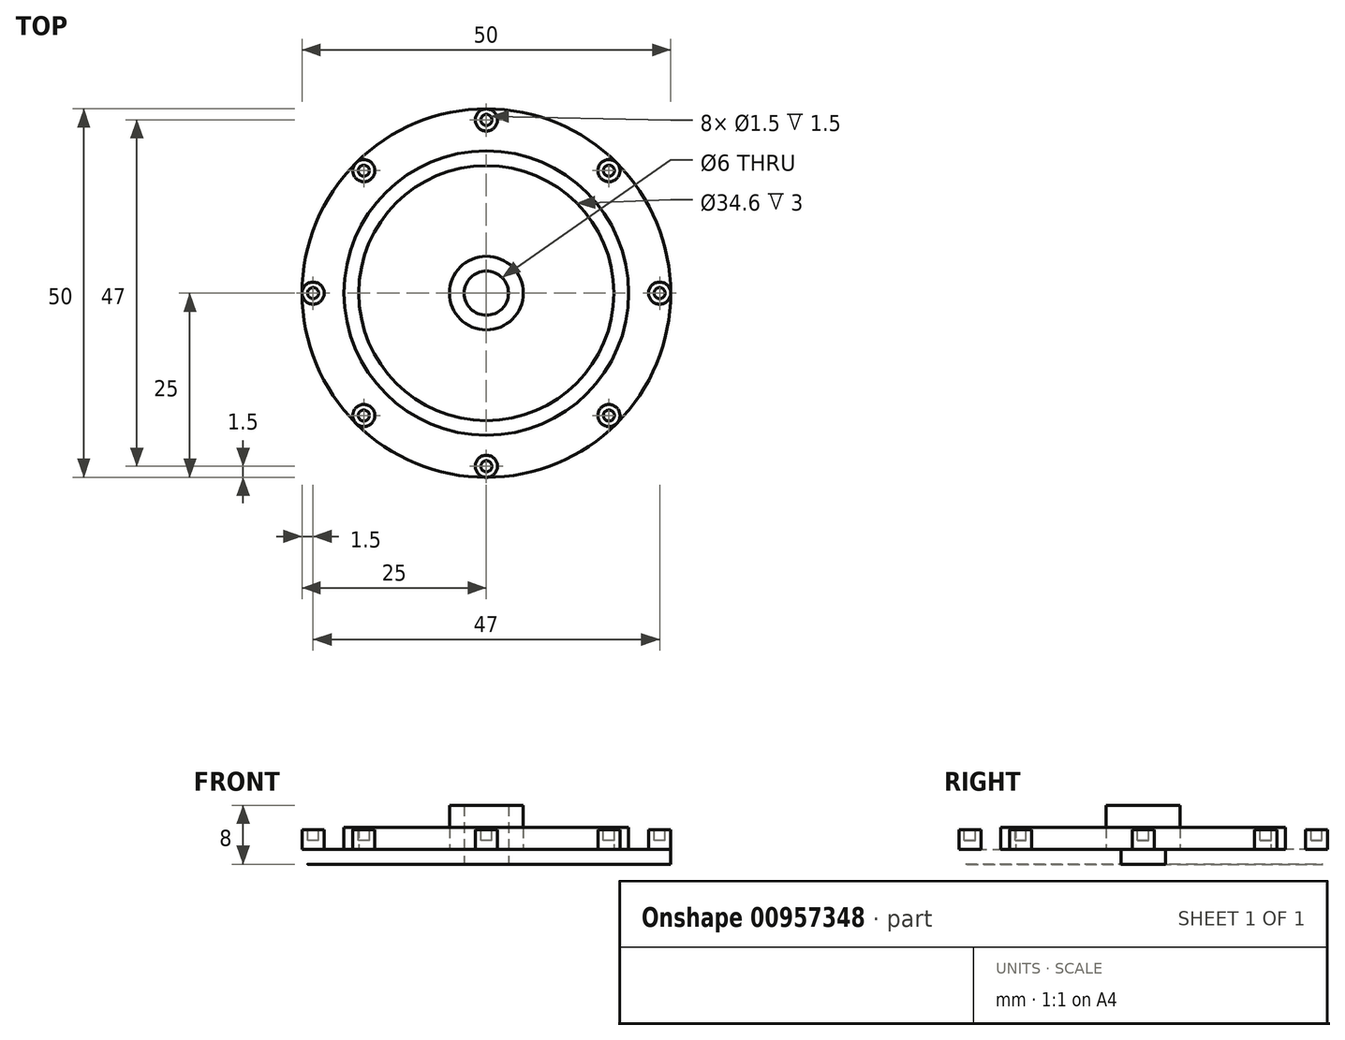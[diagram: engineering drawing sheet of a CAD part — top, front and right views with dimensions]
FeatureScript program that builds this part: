
annotation { "Feature Type Name" : "Feature", "Feature Type Description" : "" }
export const myFeature = defineFeature(function(context is Context, id is Id, definition is map)
    precondition{}
    {
        {
            var Q0;
            Q0=qCreatedBy(makeId("Top.planeOp"),FACE);
            var sketch = newSketch(context, id + "F0", { "sketchPlane" : qUnion([Q0])});
            skCircle(sketch, "E0", {"center": v(0, 0) * mm, "radius": 25 * mm});
            skCircle(sketch, "E1", {"center": v(0, 0) * mm, "radius": 3 * mm});
            skSolve(sketch);
        }
        {
            var Q0;
            Q0=makeQuery(id+"F0.imprint","IMPRINT",FACE,{"disambiguationData":[TD([[makeQuery(id+"F0.imprint","IMPRINT",EDGE,{"derivedFrom":sQuery(id+"F0.wireOp",EDGE,"E0")}),1.0]])]});
            extrude(context, id + "F1", {"entities" : qUnion([Q0]), "depth" : 2 * mm, "offsetDistance" : 25 * mm});
        }
        {
            var Q0;
            Q0=makeQuery(id+"F1.opExtrude","CAP_FACE",FACE,{"disambiguationData":[OSD([sQuery(id+"F0.wireOp",EDGE,"E0"),sQuery(id+"F0.wireOp",EDGE,"E1")])],"isStart":false});
            var sketch = newSketch(context, id + "F2", { "sketchPlane" : qUnion([Q0])});
            skCircle(sketch, "E2", {"center": v(0, 0) * mm, "radius": 19.3 * mm});
            skCircle(sketch, "E3", {"center": v(0, 0) * mm, "radius": 17.3 * mm});
            skSolve(sketch);
        }
        {
            var Q0;
            Q0=makeQuery(id+"F2.imprint","IMPRINT",FACE,{"disambiguationData":[TD([[makeQuery(id+"F2.imprint","IMPRINT",EDGE,{"derivedFrom":sQuery(id+"F2.wireOp",EDGE,"E2")}),1.0]])]});
            extrude(context, id + "F3", {"entities" : qUnion([Q0]), "operationType" : NewBodyOperationType.ADD, "depth" : 3 * mm, "offsetDistance" : 25 * mm});
        }
        {
            var Q0;
            {var subQ0=sQuery(id+"F0.wireOp",EDGE,"E0");Q0=makeQuery(id+"F3.boolean.opBoolean","SPLIT",FACE,{"disambiguationData":[TD([makeQuery(id+"F1.opExtrude","SWEPT_FACE",FACE,{"disambiguationData":[OSD([subQ0])]})])],"derivedFrom":makeQuery(id+"F1.opExtrude","CAP_FACE",FACE,{"disambiguationData":[OSD([subQ0,sQuery(id+"F0.wireOp",EDGE,"E1")])],"isStart":false})});}
            var sketch = newSketch(context, id + "F4", { "sketchPlane" : qUnion([Q0])});
            skCircle(sketch, "E4", {"center": v(0, 23.5) * mm, "radius": 1.5 * mm});
            skCircle(sketch, "E5.1.0", {"center": v(-16.62, 16.62) * mm, "radius": 1.5 * mm});
            skCircle(sketch, "E5.2.0", {"center": v(-23.5, 0) * mm, "radius": 1.5 * mm});
            skCircle(sketch, "E5.3.0", {"center": v(-16.62, -16.62) * mm, "radius": 1.5 * mm});
            skCircle(sketch, "E5.4.0", {"center": v(0, -23.5) * mm, "radius": 1.5 * mm});
            skCircle(sketch, "E5.5.0", {"center": v(16.62, -16.62) * mm, "radius": 1.5 * mm});
            skCircle(sketch, "E5.6.0", {"center": v(23.5, 0) * mm, "radius": 1.5 * mm});
            skCircle(sketch, "E5.7.0", {"center": v(16.62, 16.62) * mm, "radius": 1.5 * mm});
            skPoint(sketch, "E5.center", {"position": v(0, 0) * mm});
            skSolve(sketch);
        }
        {
            var Q0;
            Q0 = qSketchRegion(id + "F4", true);
            extrude(context, id + "F5", {"entities" : qUnion([Q0]), "operationType" : NewBodyOperationType.ADD, "depth" : 2.7 * mm, "offsetDistance" : 25 * mm});
        }
        {
            var Q0;
            {var subQ0=sQuery(id+"F0.wireOp",EDGE,"E1");Q0=makeQuery(id+"F3.boolean.opBoolean","SPLIT",FACE,{"disambiguationData":[TD([makeQuery(id+"F1.opExtrude","SWEPT_FACE",FACE,{"disambiguationData":[OSD([subQ0])]})])],"derivedFrom":makeQuery(id+"F1.opExtrude","CAP_FACE",FACE,{"disambiguationData":[OSD([sQuery(id+"F0.wireOp",EDGE,"E0"),subQ0])],"isStart":false})});}
            var sketch = newSketch(context, id + "F6", { "sketchPlane" : qUnion([Q0])});
            skCircle(sketch, "E6", {"center": v(0, 0) * mm, "radius": 5 * mm});
            skCircle(sketch, "E7.0", {"center": v(0, 0) * mm, "radius": 3 * mm});
            skSolve(sketch);
        }
        {
            var Q0;
            Q0 = qSketchRegion(id + "F6", true);
            extrude(context, id + "F7", {"entities" : qUnion([Q0]), "operationType" : NewBodyOperationType.ADD, "depth" : 6 * mm, "offsetDistance" : 25 * mm});
        }
        {
            var Q0;
            Q0=makeQuery(id+"F5.opExtrude","CAP_FACE",FACE,{"disambiguationData":[OSD([sQuery(id+"F4.wireOp",EDGE,"E5.6.0")])],"isStart":false});
            var sketch = newSketch(context, id + "F8", { "sketchPlane" : qUnion([Q0])});
            skCircle(sketch, "E8", {"center": v(23.5, 0) * mm, "radius": 0.75 * mm});
            skCircle(sketch, "E9.1.0", {"center": v(16.62, 16.62) * mm, "radius": 0.75 * mm});
            skCircle(sketch, "E9.2.0", {"center": v(0, 23.5) * mm, "radius": 0.75 * mm});
            skCircle(sketch, "E9.3.0", {"center": v(-16.62, 16.62) * mm, "radius": 0.75 * mm});
            skCircle(sketch, "E9.4.0", {"center": v(-23.5, 0) * mm, "radius": 0.75 * mm});
            skCircle(sketch, "E9.5.0", {"center": v(-16.62, -16.62) * mm, "radius": 0.75 * mm});
            skCircle(sketch, "E9.6.0", {"center": v(0, -23.5) * mm, "radius": 0.75 * mm});
            skCircle(sketch, "E9.7.0", {"center": v(16.62, -16.62) * mm, "radius": 0.75 * mm});
            skPoint(sketch, "E9.center", {"position": v(0, 0) * mm});
            skSolve(sketch);
        }
        {
            var Q0;
            Q0 = qSketchRegion(id + "F8", true);
            extrude(context, id + "F9", {"entities" : qUnion([Q0]), "operationType" : NewBodyOperationType.REMOVE, "oppositeDirection" : true, "depth" : 1.5 * mm, "offsetDistance" : 25 * mm});
        }
    });
